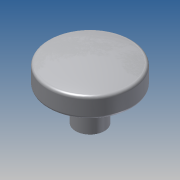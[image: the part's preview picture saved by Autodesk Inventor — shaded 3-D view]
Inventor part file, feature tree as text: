
AUTODESK INVENTOR PART (.ipt)
format: ipt  version: 2014 SP1 (Build 180222100, 222)  size: 275,456 bytes
history: native  units: in
note: dims shown in document units (in); Inventor stores cm internally (conversion verified against a paired STEP export)
features: sketch x6, extrude x5, plane x2, pattern_circular x1, revolve x1
ambient origin geometry x8: Origin, YZ Plane, XZ Plane, XY Plane, X Axis, Y Axis, Z Axis, Center Point
bodies: Solid1 (feature_tree)
feature tree (15):
  extrude  "Extrusion1"  Depth=0.05in
  sketch  "Sketch2"  dims[d2=8.0in d3=0.0in d4=0.5in]
  plane  "Work Plane1"
  extrude  "Extrusion2"  Depth=0.5in
  extrude  "Extrusion3"  Depth=0.5in
  pattern_circular  "Circular Pattern1"  Count=3 Angle=360.0deg
  plane  "Work Plane5"
  revolve  "Revolution3"  [1 undecoded]
  extrude  "Extrusion5"  Depth=4.0in
  extrude  "Extrusion6"  TaperAngle=90.0deg  [1 undecoded]
  sketch  "Sketch1"  dims[d0=6.0in d1=0.05in]
  sketch  "Sketch3"  dims[d5=0.75in d6=0.5in]
  sketch  "Sketch4"  dims[d7=0.05in d8=0.0in]
  sketch  "Sketch8"  dims[d9=0.05in]
  sketch  "Sketch11"  dims[d10=4.0in d11=0.0in d12=1.1811in d13=360.0deg d25=-0.25in d27=4.0in d30=90.0deg d34=6.5in d35=0.25in d36=0.0in d37=0.5in d38=0.0in d39=1.0in]
note: 2 required parameter values undecoded (feature->parameter linkage not recoverable at this tier; creation-order binding heuristic only, values carry confidence <= 0.55)